# Revit family: Scale-SR_Scales-SR463iR-4
name_source: partatom
category: Specialty Equipment
units: mm (PartAtom-declared; Revit-internal decimal feet)

## family parameters
Always vertical = Yes
Cut with Voids When Loaded = No
OmniClass Number = 23.40.70.11.14.11
OmniClass Title = Medical Equipment
Part Type = Normal
Room Calculation Point = No
Round Connector Dimension = Use Diameter
Shared = No
Work Plane-Based = No

## types (4) — shared parameters
Accuracy = 0.1% +/- 1 Digit of Displayed Resolution
Assembly Code = E1020810
Auto Power Down = 30 to 300 Seconds
Auto Zero = One Button Auto-Tare
Averaging = Automatic Digital Filter
BIM Version = v4.1
BIM Version Available (Earliest) = 2017
Calibration = Traceable to NIST Standards
Control Panel Offset from Center = 12"
Default Elevation = 0"
Display Resolution = 0.1 lb / 0.1 kg
Display Type = 16-Character Dot-Matrix LCD
Display Units = Pounds / Kilograms
Frame Distance to Wall = 12"
Manufacturer = SR Scales by SR Instruments, Inc.
Maximum Weight Capacity = 1000 lbs or 454 kg
Memory Recall = Recalls Last Stored Weight
Pit Depth = 3"
Platform Depth = 47 1/2"
Platform Size = 48'' x 72'' (122 cm x 183 cm)
Platform Width = 71 1/2"
Power Supply = 110v AC, 50 - 60 Hz
Product Page URL = https://srinstruments.com
URL = http://www.srinstruments.com
Wall Plate Center Elevation = 53"

## per-type parameters (varying)
| type | Description | Show Handrail | Show Printer |
| SR463iR-4 | 48" x 72" In-Floor Platform Scale | No | No |
| SR463iR-4P | 48" x 72" In-Floor Platform Scale with Printer | No | Yes |
| SR463iR-4H | 48" x 72" In-Floor Platform Scale with Handrail | Yes | No |
| SR463iR-4PH | 48" x 72" In-Floor Platform Scale with Printer and Handrail | Yes | Yes |

note: column(s) folded — value = type name in every type: Model

## geometry (parser evidence)
native form markers: Blend x1, Sweep x3
no freeform markers — native parametric forms only
